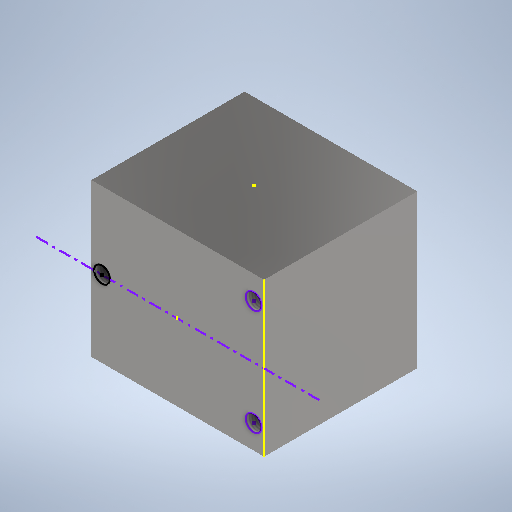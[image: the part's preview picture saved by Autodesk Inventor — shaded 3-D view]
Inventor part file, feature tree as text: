
AUTODESK INVENTOR PART (.ipt)
format: ipt  version: 2025.1 (Build 291241000, 241)  size: 257,536 bytes
history: native  units: mm
features: thread x6, sketch x6, extrude x3, plane x1
ambient origin geometry x8: Origin, YZ Plane, XZ Plane, XY Plane, X Axis, Y Axis, Z Axis, Center Point
bodies: Solid1 (feature_tree)
feature tree (16):
  extrude  "Extrusion1"  Depth=29.0mm
  extrude  "Extrusion2"  Depth=3.0mm
  thread  "Thread1"  [1 undecoded]
  thread  "Thread2"  [1 undecoded]
  thread  "Thread3"  [1 undecoded]
  sketch  "Sketch3"  dims[d8=2.0mm d9=28.7mm d10=4.0mm d11=0.0mm d12=5.0mm d13=0.0mm d14=5.0mm d15=0.0mm]
  sketch  "Sketch4"  dims[d16=5.0mm d17=0.0mm]
  plane  "Work Plane2"
  sketch  "Sketch6"  dims[d19=-29.0mm]
  sketch  "Sketch7"  dims[d20=3.0mm d21=3.0mm d22=3.0mm d23=3.0mm d24=0.0mm d25=5.0mm d26=0.0mm d27=5.0mm d28=0.0mm d29=5.0mm d30=0.0mm]
  extrude  "Extrusion3"  Depth=4.0mm
  thread  "Thread4"  [1 undecoded]
  thread  "Thread5"  [1 undecoded]
  thread  "Thread6"  [1 undecoded]
  sketch  "Sketch1"  dims[d0=32.7mm d1=29.0mm]
  sketch  "Sketch2"  dims[d2=29.0mm d3=0.0mm d4=3.0mm d5=3.0mm d6=3.0mm d7=20.0mm]
note: 6 required parameter values undecoded (feature->parameter linkage not recoverable at this tier; creation-order binding heuristic only, values carry confidence <= 0.55)
